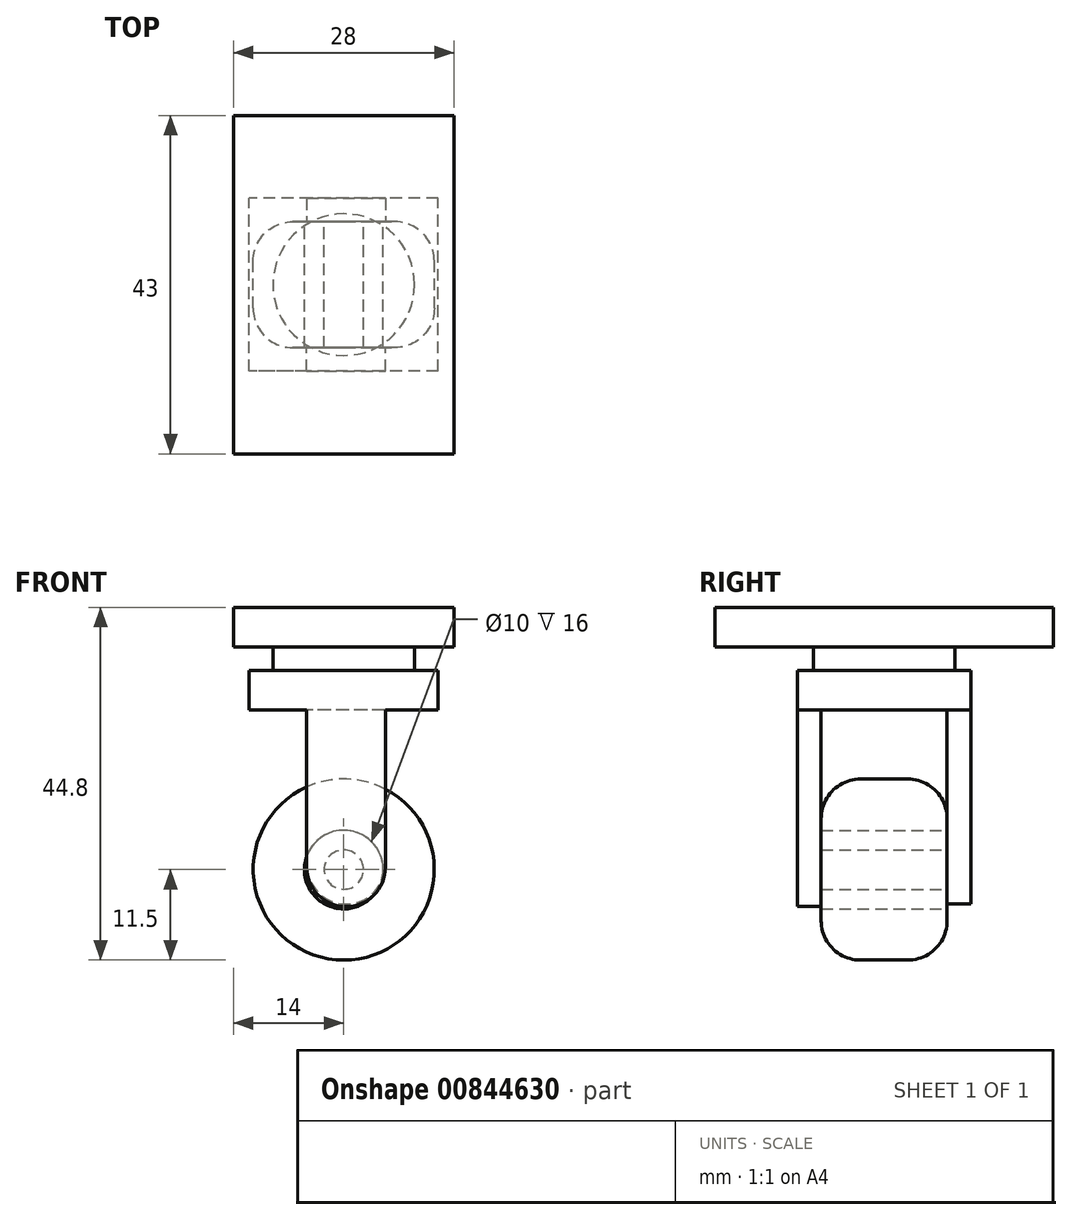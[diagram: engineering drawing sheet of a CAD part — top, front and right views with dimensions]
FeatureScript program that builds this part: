
annotation { "Feature Type Name" : "Feature", "Feature Type Description" : "" }
export const myFeature = defineFeature(function(context is Context, id is Id, definition is map)
    precondition{}
    {
        {
            var Q0;
            Q0=qCreatedBy(makeId("Front.planeOp"),FACE);
            var sketch = newSketch(context, id + "F0", { "sketchPlane" : qUnion([Q0])});
            skCircle(sketch, "E0", {"center": v(0, 0) * mm, "radius": 11.5 * mm});
            skCircle(sketch, "E1", {"center": v(0, 0) * mm, "radius": 2.5 * mm});
            skCircle(sketch, "E2", {"center": v(0, 0) * mm, "radius": 5 * mm});
            skSolve(sketch);
        }
        {
            var Q0;
            Q0=makeQuery(id+"F0.imprint","IMPRINT",FACE,{"disambiguationData":[TD([[makeQuery(id+"F0.imprint","IMPRINT",EDGE,{"derivedFrom":sQuery(id+"F0.wireOp",EDGE,"E1")}),1.0]])]});
            var Q1;
            Q1=makeQuery(id+"F0.imprint","IMPRINT",FACE,{"disambiguationData":[TD([[makeQuery(id+"F0.imprint","IMPRINT",EDGE,{"derivedFrom":sQuery(id+"F0.wireOp",EDGE,"E0")}),1.0]])]});
            extrude(context, id + "F1", {"entities" : qUnion([Q0, Q1]), "depth" : 16 * mm, "offsetDistance" : 25 * mm, "symmetric" : true});
        }
        {
            var Q0;
            Q0=makeQuery(id+"F1.opExtrude","SWEPT_FACE",FACE,{"disambiguationData":[OSD([sQuery(id+"F0.wireOp",EDGE,"E0")])]});
            var Q1;
            Q1=makeQuery(id+"F1.opExtrude","CAP_EDGE",EDGE,{"disambiguationData":[OSD([sQuery(id+"F0.wireOp",EDGE,"E0")])],"isStart":false});
            fillet(context, id + "F2", {"entities" : qUnion([Q0, Q1]), "radius" : 5 * mm, "tangentPropagation" : true, "allowEdgeOverflow" : false});
        }
        {
            var Q0;
            Q0=makeQuery(id+"F1.opExtrude","CAP_FACE",FACE,{"disambiguationData":[OSD([sQuery(id+"F0.wireOp",EDGE,"E1")])],"isStart":false});
            var sketch = newSketch(context, id + "F3", { "sketchPlane" : qUnion([Q0])});
            skLineSegment(sketch, "E3.bottom", {"start": v(5.3, 20.3) * mm, "end": v(-4.7, 20.3) * mm});
            skLineSegment(sketch, "E3.left", {"start": v(5.3, 20.3) * mm, "end": v(5.3, -4.7) * mm});
            skLineSegment(sketch, "E3.right", {"start": v(-4.7, 20.3) * mm, "end": v(-4.7, -4.7) * mm});
            skPoint(sketch, "E3.middle", {"position": v(0, 0) * mm});
            skLineSegment(sketch, "E4", {"start": v(-4.7, -4.7) * mm, "end": v(5.3, -4.7) * mm});
            skSolve(sketch);
        }
        {
            var Q0;
            Q0=makeQuery(id+"F3.imprint","IMPRINT",FACE,{"disambiguationData":[TD([[makeQuery(id+"F3.imprint","IMPRINT",EDGE,{"derivedFrom":makeQuery(id+"F1.opExtrude","CAP_EDGE",EDGE,{"disambiguationData":[OSD([sQuery(id+"F0.wireOp",EDGE,"E1")])],"isStart":false})}),1.0]])]});
            var Q1;
            Q1=makeQuery(id+"F3.imprint","IMPRINT",FACE,{"disambiguationData":[TD([[makeQuery(id+"F3.imprint","IMPRINT",EDGE,{"derivedFrom":sQuery(id+"F3.wireOp",EDGE,"E3.bottom")}),1.0]])]});
            extrude(context, id + "F4", {"entities" : qUnion([Q0, Q1]), "depth" : 3 * mm, "offsetDistance" : 25 * mm});
        }
        {
            var Q0;
            Q0=makeQuery(id+"F4.opExtrude","SWEPT_EDGE",EDGE,{"disambiguationData":[OSD([sQuery(id+"F3.wireOp",EDGE,"E3.right"),sQuery(id+"F3.wireOp",EDGE,"E4")])]});
            var Q1;
            Q1=makeQuery(id+"F4.opExtrude","SWEPT_EDGE",EDGE,{"disambiguationData":[OSD([sQuery(id+"F3.wireOp",EDGE,"E3.left"),sQuery(id+"F3.wireOp",EDGE,"E4")])]});
            fillet(context, id + "F5", {"entities" : qUnion([Q0, Q1]), "radius" : 5 * mm, "tangentPropagation" : true, "allowEdgeOverflow" : false});
        }
        {
            var Q0;
            Q0=makeQuery(id+"F4.opExtrude","SWEPT_FACE",FACE,{"disambiguationData":[OSD([sQuery(id+"F3.wireOp",EDGE,"E3.bottom")])]});
            var sketch = newSketch(context, id + "F6", { "sketchPlane" : qUnion([Q0])});
            skLineSegment(sketch, "E5.bottom", {"start": v(12, -11) * mm, "end": v(-12, -11) * mm});
            skLineSegment(sketch, "E5.top", {"start": v(12, 11) * mm, "end": v(-12, 11) * mm});
            skLineSegment(sketch, "E5.left", {"start": v(12, -11) * mm, "end": v(12, 11) * mm});
            skLineSegment(sketch, "E5.right", {"start": v(-12, -11) * mm, "end": v(-12, 11) * mm});
            skPoint(sketch, "E5.middle", {"position": v(0, 0) * mm});
            skSolve(sketch);
        }
        {
            var Q0;
            Q0=makeQuery(id+"F6.imprint","IMPRINT",FACE,{"disambiguationData":[TD([[makeQuery(id+"F6.imprint","IMPRINT",EDGE,{"derivedFrom":sQuery(id+"F6.wireOp",EDGE,"E5.top")}),1.0]])]});
            var Q1;
            {var subQ1=sQuery(id+"F3.wireOp",EDGE,"E3.bottom");Q1=makeQuery(id+"F6.imprint","IMPRINT",FACE,{"disambiguationData":[TD([[makeQuery(id+"F6.imprint","IMPRINT",EDGE,{"derivedFrom":makeQuery(id+"F4.opExtrude","CAP_EDGE",EDGE,{"disambiguationData":[OSD([subQ1])],"isStart":true})}),1.0]])]});}
            extrude(context, id + "F7", {"entities" : qUnion([Q0, Q1]), "operationType" : NewBodyOperationType.ADD, "depth" : 5 * mm, "offsetDistance" : 25 * mm});
        }
        {
            var Q0;
            Q0=makeQuery(id+"F1.opExtrude","CAP_FACE",FACE,{"disambiguationData":[OSD([sQuery(id+"F0.wireOp",EDGE,"E1")])],"isStart":true});
            var sketch = newSketch(context, id + "F8", { "sketchPlane" : qUnion([Q0])});
            skLineSegment(sketch, "E6", {"start": v(-5.3, 20.3) * mm, "end": v(-5.3, 4.37) * mm});
            skLineSegment(sketch, "E7", {"start": v(4.7, 20.3) * mm, "end": v(4.7, -4.37) * mm});
            skLineSegment(sketch, "E8", {"start": v(4.7, 20.3) * mm, "end": v(-5.3, 20.3) * mm});
            skLineSegment(sketch, "E9.bottom", {"start": v(4.7, -4.37) * mm, "end": v(-5.3, -4.37) * mm});
            skLineSegment(sketch, "E9.left", {"start": v(4.7, -4.37) * mm, "end": v(4.7, 4.37) * mm});
            skPoint(sketch, "E9.middle", {"position": v(0, 0) * mm});
            skLineSegment(sketch, "E10", {"start": v(-5.3, 4.37) * mm, "end": v(-5.3, -4.37) * mm});
            skSolve(sketch);
        }
        {
            var Q0;
            Q0=makeQuery(id+"F8.imprint","IMPRINT",FACE,{"disambiguationData":[TD([[makeQuery(id+"F8.imprint","IMPRINT",EDGE,{"derivedFrom":sQuery(id+"F8.wireOp",EDGE,"E6")}),1.0]])]});
            var Q1;
            Q1=makeQuery(id+"F8.imprint","IMPRINT",FACE,{"disambiguationData":[TD([[makeQuery(id+"F8.imprint","IMPRINT",EDGE,{"derivedFrom":makeQuery(id+"F1.opExtrude","CAP_EDGE",EDGE,{"disambiguationData":[OSD([sQuery(id+"F0.wireOp",EDGE,"E1")])],"isStart":true})}),-1.0]])]});
            extrude(context, id + "F9", {"entities" : qUnion([Q0, Q1]), "depth" : 3 * mm, "offsetDistance" : 25 * mm});
        }
        {
            var Q0;
            Q0=makeQuery(id+"F9.opExtrude","SWEPT_EDGE",EDGE,{"disambiguationData":[OSD([sQuery(id+"F8.wireOp",EDGE,"E9.bottom"),sQuery(id+"F8.wireOp",EDGE,"E10")])]});
            var Q1;
            Q1=makeQuery(id+"F9.opExtrude","SWEPT_EDGE",EDGE,{"disambiguationData":[OSD([sQuery(id+"F8.wireOp",EDGE,"E9.bottom"),sQuery(id+"F8.wireOp",EDGE,"E9.left")])]});
            fillet(context, id + "F10", {"entities" : qUnion([Q0, Q1]), "radius" : 5 * mm, "tangentPropagation" : true, "allowEdgeOverflow" : false});
        }
        {
            var Q0;
            Q0=makeQuery(id+"F7.opExtrude","CAP_FACE",FACE,{"disambiguationData":[OSD([sQuery(id+"F6.wireOp",EDGE,"E5.bottom"),sQuery(id+"F6.wireOp",EDGE,"E5.top"),sQuery(id+"F6.wireOp",EDGE,"E5.left"),sQuery(id+"F6.wireOp",EDGE,"E5.right")])],"isStart":false});
            var sketch = newSketch(context, id + "F11", { "sketchPlane" : qUnion([Q0])});
            skCircle(sketch, "E11", {"center": v(0, 0) * mm, "radius": 9 * mm});
            skSolve(sketch);
        }
        {
            var Q0;
            Q0=makeQuery(id+"F11.imprint","IMPRINT",FACE,{"disambiguationData":[TD([[makeQuery(id+"F11.imprint","IMPRINT",EDGE,{"derivedFrom":sQuery(id+"F11.wireOp",EDGE,"E11")}),1.0]])]});
            extrude(context, id + "F12", {"entities" : qUnion([Q0]), "operationType" : NewBodyOperationType.ADD, "depth" : 3 * mm, "offsetDistance" : 25 * mm});
        }
        {
            var Q0;
            Q0=makeQuery(id+"F12.opExtrude","CAP_FACE",FACE,{"disambiguationData":[OSD([sQuery(id+"F11.wireOp",EDGE,"E11")])],"isStart":false});
            var sketch = newSketch(context, id + "F13", { "sketchPlane" : qUnion([Q0])});
            skLineSegment(sketch, "E12.bottom", {"start": v(14, -21.5) * mm, "end": v(-14, -21.5) * mm});
            skLineSegment(sketch, "E12.top", {"start": v(14, 21.5) * mm, "end": v(-14, 21.5) * mm});
            skLineSegment(sketch, "E12.left", {"start": v(14, -21.5) * mm, "end": v(14, 21.5) * mm});
            skLineSegment(sketch, "E12.right", {"start": v(-14, -21.5) * mm, "end": v(-14, 21.5) * mm});
            skPoint(sketch, "E12.middle", {"position": v(0, 0) * mm});
            skSolve(sketch);
        }
        {
            var Q0;
            Q0=makeQuery(id+"F13.imprint","IMPRINT",FACE,{"disambiguationData":[TD([[makeQuery(id+"F13.imprint","IMPRINT",EDGE,{"derivedFrom":makeQuery(id+"F12.opExtrude","CAP_EDGE",EDGE,{"disambiguationData":[OSD([sQuery(id+"F11.wireOp",EDGE,"E11")])],"isStart":false})}),1.0]])]});
            var Q1;
            Q1=makeQuery(id+"F13.imprint","IMPRINT",FACE,{"disambiguationData":[TD([[makeQuery(id+"F13.imprint","IMPRINT",EDGE,{"derivedFrom":sQuery(id+"F13.wireOp",EDGE,"E12.bottom")}),-1.0]])]});
            extrude(context, id + "F14", {"entities" : qUnion([Q0, Q1]), "operationType" : NewBodyOperationType.ADD, "depth" : 5 * mm, "offsetDistance" : 25 * mm});
        }
    });
